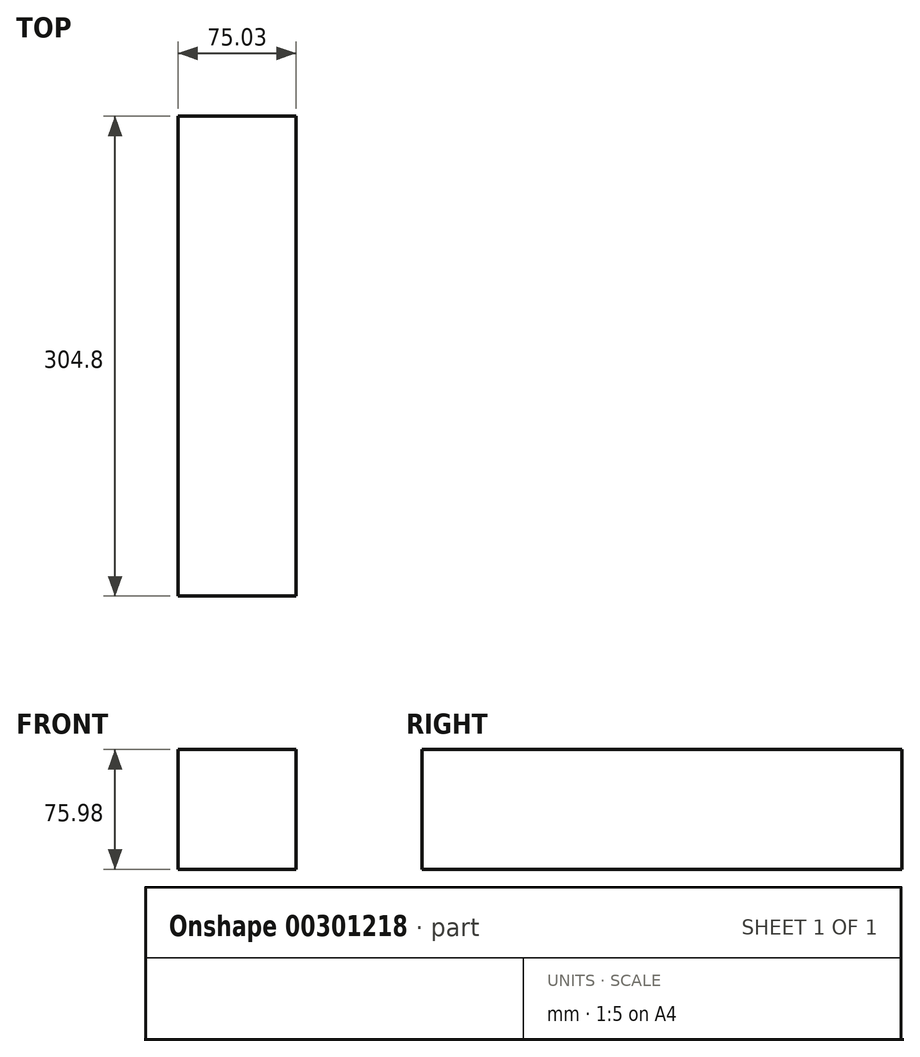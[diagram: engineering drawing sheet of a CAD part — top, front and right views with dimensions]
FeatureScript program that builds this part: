
annotation { "Feature Type Name" : "Feature", "Feature Type Description" : "" }
export const myFeature = defineFeature(function(context is Context, id is Id, definition is map)
    precondition{}
    {
        {
            var Q0;
            Q0=qCreatedBy(makeId("Front.planeOp"),FACE);
            var sketch = newSketch(context, id + "F0", { "sketchPlane" : qUnion([Q0])});
            skLineSegment(sketch, "E0.bottom", {"start": v(-75.03, 75.98) * mm, "end": v(0, 75.98) * mm});
            skLineSegment(sketch, "E0.top", {"start": v(-75.03, 0) * mm, "end": v(0, 0) * mm});
            skLineSegment(sketch, "E0.left", {"start": v(-75.03, 75.98) * mm, "end": v(-75.03, 0) * mm});
            skLineSegment(sketch, "E0.right", {"start": v(0, 75.98) * mm, "end": v(0, 0) * mm});
            skSolve(sketch);
        }
        {
            var Q0;
            Q0=makeQuery(id+"F0.imprint","IMPRINT",FACE,{"disambiguationData":[TD([[makeQuery(id+"F0.imprint","IMPRINT",EDGE,{"derivedFrom":sQuery(id+"F0.wireOp",EDGE,"E0.bottom")}),-1.0]])]});
            extrude(context, id + "F1", {"entities" : qUnion([Q0]), "depth" : 304.8 * mm});
        }
    });
